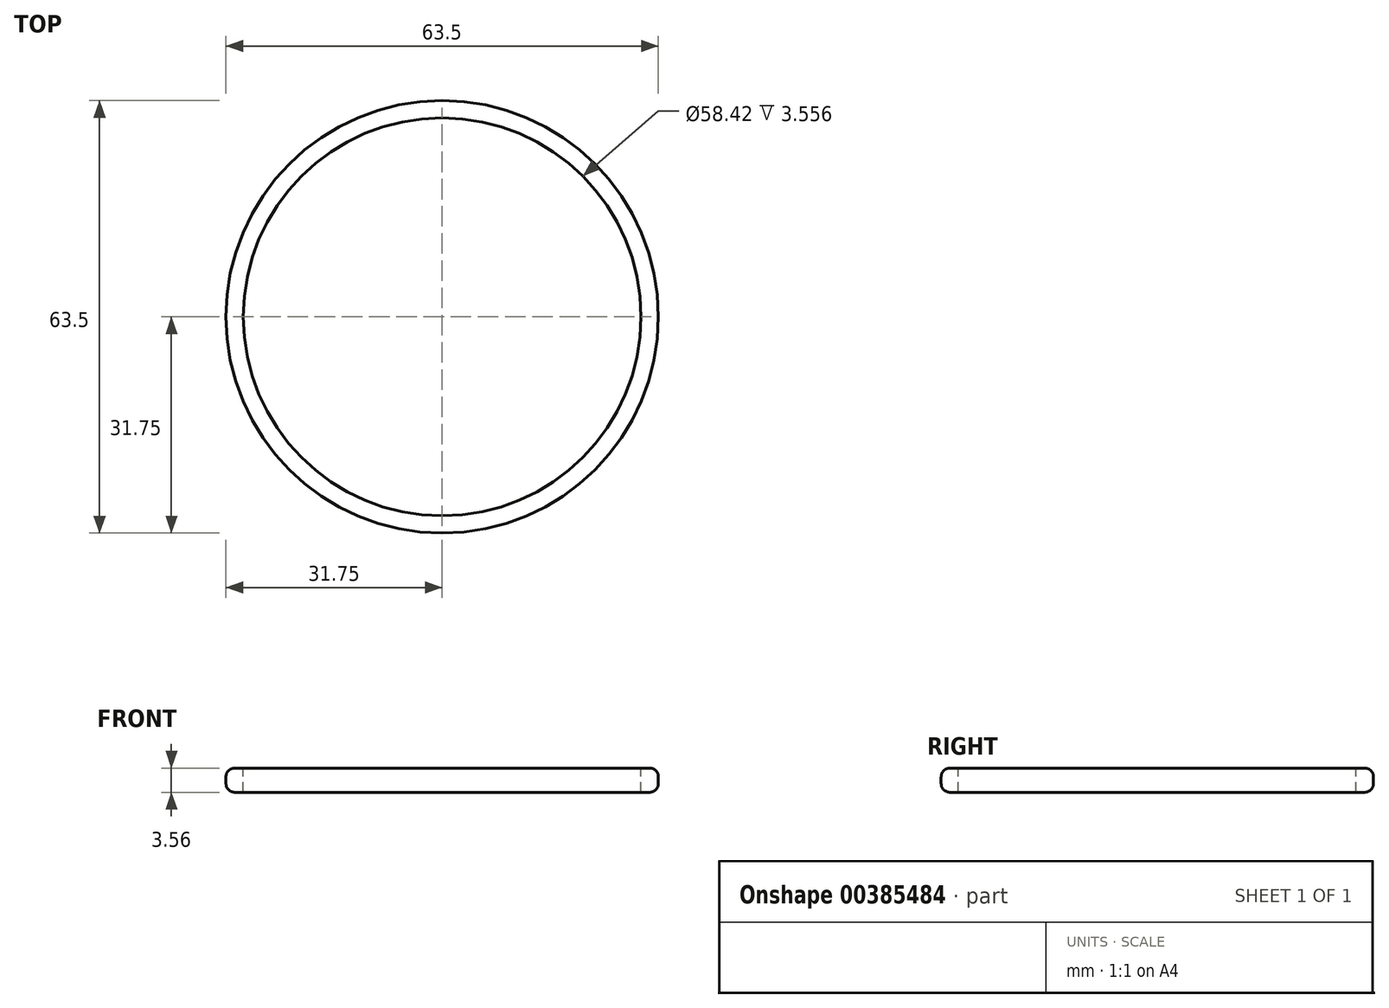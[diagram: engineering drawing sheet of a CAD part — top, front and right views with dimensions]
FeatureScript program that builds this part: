
annotation { "Feature Type Name" : "Feature", "Feature Type Description" : "" }
export const myFeature = defineFeature(function(context is Context, id is Id, definition is map)
    precondition{}
    {
        {
            var Q0;
            Q0=qCreatedBy(makeId("Top.planeOp"),FACE);
            var sketch = newSketch(context, id + "F0", { "sketchPlane" : qUnion([Q0])});
            skCircle(sketch, "E0", {"center": v(0, 0) * mm, "radius": 31.75 * mm});
            skSolve(sketch);
        }
        {
            var Q0;
            Q0=makeQuery(id+"F0.imprint","IMPRINT",FACE,{"disambiguationData":[TD([[makeQuery(id+"F0.imprint","IMPRINT",EDGE,{"derivedFrom":sQuery(id+"F0.wireOp",EDGE,"E0")}),1.0]])]});
            extrude(context, id + "F1", {"entities" : qUnion([Q0]), "depth" : 3.56 * mm});
        }
        {
            var Q0;
            Q0=makeQuery(id+"F1.opExtrude","CAP_FACE",FACE,{"disambiguationData":[OSD([sQuery(id+"F0.wireOp",EDGE,"E0")])],"isStart":false});
            var sketch = newSketch(context, id + "F2", { "sketchPlane" : qUnion([Q0])});
            skPoint(sketch, "E1", {"position": v(0, 0) * mm});
            skSolve(sketch);
        }
        {
            var Q0;
            Q0=sQuery(id+"F2.wireOp",VERTEX,"E1");
            var Q1;
            Q1=makeQuery(id+"F1.opExtrude","SWEPT_BODY",BODY,{"disambiguationData":[OSD([sQuery(id+"F0.wireOp",EDGE,"E0")])]});
            hole(context, id + "F3", {"style" : HoleStyle.SIMPLE, "endStyle" : HoleEndStyle.BLIND, "holeDiameter" : 58.42 * mm, "holeDepth" : 5.08 * mm, "isTappedThrough" : true, "tappedDepth" : 12.7 * mm, "tapClearance" : 3, "locations" : qUnion([Q0]), "scope" : qUnion([Q1])});
        }
        {
            var Q0;
            Q0=makeQuery(id+"F1.opExtrude","CAP_EDGE",EDGE,{"disambiguationData":[OSD([sQuery(id+"F0.wireOp",EDGE,"E0")])],"isStart":true});
            var Q1;
            Q1=makeQuery(id+"F3.hole-0.boolean.opBoolean","INTERSECT",EDGE,{"derivedFrom":[makeQuery(id+"F1.opExtrude","CAP_FACE",FACE,{"disambiguationData":[OSD([sQuery(id+"F0.wireOp",EDGE,"E0")])],"isStart":true}),makeQuery(id+"F3.hole-0.opRevolve","SWEPT_FACE",FACE,{"disambiguationData":[OSD([sQuery(id+"F3.hole-0.sketch.wireOp",EDGE,"core_line_1")])]})]});
            var Q2;
            Q2=makeQuery(id+"F1.opExtrude","CAP_EDGE",EDGE,{"disambiguationData":[OSD([sQuery(id+"F0.wireOp",EDGE,"E0")])],"isStart":false});
            var Q3;
            Q3=makeQuery(id+"F3.hole-0.boolean.opBoolean","COPY",EDGE,{"derivedFrom":makeQuery(id+"F3.hole-0.opRevolve","SWEPT_EDGE",EDGE,{"disambiguationData":[OSD([sQuery(id+"F3.hole-0.sketch.wireOp",EDGE,"core_line_2"),sQuery(id+"F3.hole-0.sketch.wireOp",EDGE,"core_line_3")])]})});
            fillet(context, id + "F4", {"entities" : qUnion([Q0, Q1, Q2, Q3]), "radius" : 1.27 * mm, "tangentPropagation" : true, "allowEdgeOverflow" : false});
        }
    });
